# Revit family: Shower-Sytems-American_Standard-Universal-1662609_Series
name_source: partatom
category: Plumbing Fixtures
units: mm (PartAtom-declared; Revit-internal decimal feet)

## family parameters
Cut with Voids When Loaded = No
Host = Face
OmniClass Number = 23.45.05.14.17
OmniClass Title = Showers
Part Type = Normal
Room Calculation Point = No
Round Connector Dimension = Use Diameter
Shared = Yes

## types (3) — shared parameters
1660609 -  Hand Shower = Yes
8888035 - Hose = Yes
8888036 - Wall Bracket = Yes
8888068 - Wall Union = Yes
Assembly Code = D2010700
CEC Compliant = Yes
CW Connection = No
CWFU = 3
CalGreen Compliant = Yes
Default Elevation = 44"
Description = Contemporary Hand Shower Kit 1.8 gpm/6.8 L/min
Flow Rate = 1.8 gpm/6.8 L/min
HW Connection = No
HWFU = 3
Installation Type = Wall Mounted
Manufacturer = American Standard
Material - Head Top = Rubber-American Standard-Grey
Price = Prices may vary. Please consult Manufacturer Representative for most up-to-date price list.
Product Documentation Link = https://americanstandard.box.com
Product Page URL = https://www.americanstandard-us.com
Revised Date = 08/05/2022
Tempered Water Connection = Yes
Tempered Water Connection Diameter = 1/2"
Tempered Water Connection Radius = 1/4"
URL = https://www.americanstandard-us.com
Vent Connection = No
WFU = 4
Warranty Information = One Year Limited Warranty
Waste Connection = No

## per-type parameters (varying)
| type | Finish | Material |
| 1662609.002 | Brass-American Standard-002-Polished Chrome | Brass-American Standard-002-Polished Chrome |
| 1662609.243 | Brass-American Standard-243-Matte Black | Brass-American Standard-243-Matte Black |
| 1662609.295 | Brass-American Standard-295-Brushed Nickel | Brass-American Standard-295-Brushed Nickel |

note: column(s) folded — value = type name in every type: Model

## geometry (parser evidence)
native form markers: Sweep x3
no freeform markers — native parametric forms only
